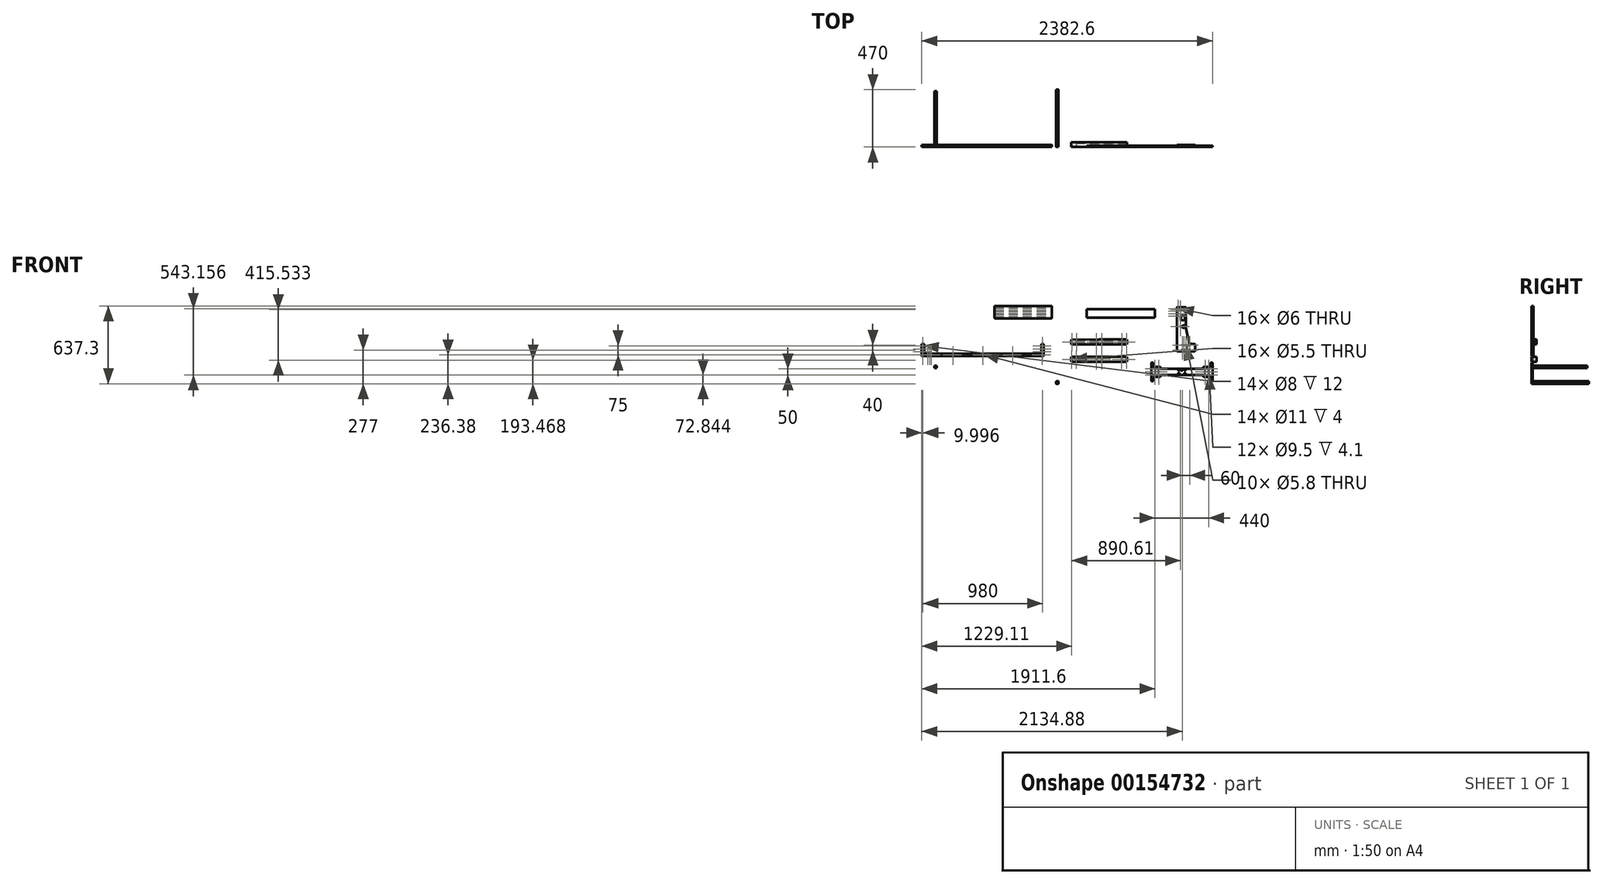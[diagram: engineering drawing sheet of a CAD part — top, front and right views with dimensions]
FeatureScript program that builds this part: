
annotation { "Feature Type Name" : "Feature", "Feature Type Description" : "" }
export const myFeature = defineFeature(function(context is Context, id is Id, definition is map)
    precondition{}
    {
        {
            var Q0;
            Q0=qCreatedBy(makeId("Front.planeOp"),FACE);
            var sketch = newSketch(context, id + "F0", { "sketchPlane" : qUnion([Q0])});
            skLineSegment(sketch, "E0.bottom", {"start": v(1.58, 127.3) * mm, "end": v(230.58, 127.3) * mm});
            skLineSegment(sketch, "E0.top", {"start": v(-227.42, 86.08) * mm, "end": v(230.58, 86.08) * mm});
            skLineSegment(sketch, "E1.0", {"start": v(225.58, 126) * mm, "end": v(225.58, 86) * mm, "construction": true});
            skLineSegment(sketch, "E2.0", {"start": v(187.58, 126) * mm, "end": v(187.58, 86) * mm, "construction": true});
            skCircle(sketch, "E3", {"center": v(187.58, 106) * mm, "radius": 2.75 * mm});
            skCircle(sketch, "E4", {"center": v(225.58, 106) * mm, "radius": 2.75 * mm});
            skLineSegment(sketch, "E5.0", {"start": v(-222.42, 126) * mm, "end": v(-222.42, 86) * mm, "construction": true});
            skLineSegment(sketch, "E6.0", {"start": v(-184.42, 126) * mm, "end": v(-184.42, 86) * mm, "construction": true});
            skCircle(sketch, "E7", {"center": v(-222.42, 106) * mm, "radius": 2.75 * mm});
            skCircle(sketch, "E8", {"center": v(-184.42, 106) * mm, "radius": 2.75 * mm});
            skLineSegment(sketch, "E9", {"start": v(1.58, 86.08) * mm, "end": v(1.58, 127.3) * mm, "construction": true});
            skLineSegment(sketch, "E10.0", {"start": v(24.58, 86) * mm, "end": v(24.58, 126) * mm, "construction": true});
            skLineSegment(sketch, "E11.0", {"start": v(-21.42, 86) * mm, "end": v(-21.42, 126) * mm, "construction": true});
            skCircle(sketch, "E12", {"center": v(24.58, 106) * mm, "radius": 3.3 * mm});
            skCircle(sketch, "E13", {"center": v(-21.42, 106) * mm, "radius": 3.3 * mm});
            skLineSegment(sketch, "E14", {"start": v(1.58, 127.3) * mm, "end": v(-227.42, 126.08) * mm});
            skLineSegment(sketch, "E15", {"start": v(-227.42, 126.08) * mm, "end": v(-227.42, 86.08) * mm});
            skLineSegment(sketch, "E16", {"start": v(230.58, 86.08) * mm, "end": v(230.58, 127.3) * mm});
            skSolve(sketch);
        }
        {
            var Q0;
            Q0=makeQuery(id+"F0.imprint","IMPRINT",FACE,{"disambiguationData":[TD([[makeQuery(id+"F0.imprint","IMPRINT",EDGE,{"derivedFrom":sQuery(id+"F0.wireOp",EDGE,"E13")}),1.0]])]});
            var Q1;
            Q1=makeQuery(id+"F0.imprint","IMPRINT",FACE,{"disambiguationData":[TD([[makeQuery(id+"F0.imprint","IMPRINT",EDGE,{"derivedFrom":sQuery(id+"F0.wireOp",EDGE,"E12")}),1.0]])]});
            var Q2;
            Q2=makeQuery(id+"F0.imprint","IMPRINT",FACE,{"disambiguationData":[TD([[makeQuery(id+"F0.imprint","IMPRINT",EDGE,{"derivedFrom":sQuery(id+"F0.wireOp",EDGE,"E8")}),1.0]])]});
            var Q3;
            Q3=makeQuery(id+"F0.imprint","IMPRINT",FACE,{"disambiguationData":[TD([[makeQuery(id+"F0.imprint","IMPRINT",EDGE,{"derivedFrom":sQuery(id+"F0.wireOp",EDGE,"E7")}),1.0]])]});
            var Q4;
            Q4=makeQuery(id+"F0.imprint","IMPRINT",FACE,{"disambiguationData":[TD([[makeQuery(id+"F0.imprint","IMPRINT",EDGE,{"derivedFrom":sQuery(id+"F0.wireOp",EDGE,"E0.bottom")}),-1.0]])]});
            var Q5;
            Q5=makeQuery(id+"F0.imprint","IMPRINT",FACE,{"disambiguationData":[TD([[makeQuery(id+"F0.imprint","IMPRINT",EDGE,{"derivedFrom":sQuery(id+"F0.wireOp",EDGE,"E3")}),1.0]])]});
            var Q6;
            Q6=makeQuery(id+"F0.imprint","IMPRINT",FACE,{"disambiguationData":[TD([[makeQuery(id+"F0.imprint","IMPRINT",EDGE,{"derivedFrom":sQuery(id+"F0.wireOp",EDGE,"E4")}),1.0]])]});
            extrude(context, id + "F1", {"entities" : qUnion([Q0, Q1, Q2, Q3, Q4, Q5, Q6]), "oppositeDirection" : true, "depth" : 40 * mm});
        }
        {
            var Q0;
            Q0=sQuery(id+"F0.wireOp",VERTEX,"E13.center");
            var Q1;
            Q1=sQuery(id+"F0.wireOp",VERTEX,"E12.center");
            var Q2;
            Q2=sQuery(id+"F0.wireOp",VERTEX,"E7.center");
            var Q3;
            Q3=sQuery(id+"F0.wireOp",VERTEX,"E8.center");
            var Q4;
            Q4=sQuery(id+"F0.wireOp",VERTEX,"E3.center");
            var Q5;
            Q5=sQuery(id+"F0.wireOp",VERTEX,"E4.center");
            var Q6;
            Q6=makeQuery(id+"F1.opExtrude","SWEPT_BODY",BODY,{"disambiguationData":[OSD([sQuery(id+"F0.wireOp",EDGE,"E0.bottom"),sQuery(id+"F0.wireOp",EDGE,"E0.top"),sQuery(id+"F0.wireOp",EDGE,"E0.left"),sQuery(id+"F0.wireOp",EDGE,"E0.right")])]});
            hole(context, id + "F2", {"style" : HoleStyle.SIMPLE, "endStyle" : HoleEndStyle.BLIND, "holeDiameter" : 5.5 * mm, "holeDepth" : 15 * mm, "locations" : qUnion([Q0, Q1, Q2, Q3, Q4, Q5]), "scope" : qUnion([Q6])});
        }
        {
            var Q0;
            Q0=makeQuery(id+"F1.opExtrude","SWEPT_FACE",FACE,{"disambiguationData":[OSD([sQuery(id+"F0.wireOp",EDGE,"E15")])]});
            var sketch = newSketch(context, id + "F3", { "sketchPlane" : qUnion([Q0])});
            skLineSegment(sketch, "E17.0", {"start": v(-20, 126.08) * mm, "end": v(-20, 86.08) * mm, "construction": true});
            skCircle(sketch, "E18", {"center": v(-30, 121.08) * mm, "radius": 3.4 * mm, "construction": true});
            skCircle(sketch, "E19.0.1.0", {"center": v(-30, 106.08) * mm, "radius": 3.4 * mm, "construction": true});
            skCircle(sketch, "E19.0.2.0", {"center": v(-30, 91.08) * mm, "radius": 3.4 * mm, "construction": true});
            skLineSegment(sketch, "E19.direction1", {"start": v(-30, 121.08) * mm, "end": v(-5, 121.08) * mm, "construction": true});
            skLineSegment(sketch, "E19.direction2", {"start": v(-30, 121.08) * mm, "end": v(-30, 106.08) * mm, "construction": true});
            skSolve(sketch);
        }
        {
            var Q0;
            Q0=sQuery(id+"F3.wireOp",VERTEX,"E18.center");
            var Q1;
            Q1=sQuery(id+"F3.wireOp",VERTEX,"E19.0.1.0.center");
            var Q2;
            Q2=sQuery(id+"F3.wireOp",VERTEX,"E19.0.2.0.center");
            var Q3;
            Q3=makeQuery(id+"F1.opExtrude","SWEPT_BODY",BODY,{"disambiguationData":[OSD([sQuery(id+"F0.wireOp",EDGE,"E0.bottom"),sQuery(id+"F0.wireOp",EDGE,"E0.top"),sQuery(id+"F0.wireOp",EDGE,"E14"),sQuery(id+"F0.wireOp",EDGE,"E15"),sQuery(id+"F0.wireOp",EDGE,"E16")])]});
            hole(context, id + "F4", {"style" : HoleStyle.SIMPLE, "endStyle" : HoleEndStyle.THROUGH, "holeDiameter" : 8 * mm, "locations" : qUnion([Q0, Q1, Q2]), "scope" : qUnion([Q3]), "isTappedThrough" : true});
        }
        {
            var Q0;
            Q0=qCreatedBy(makeId("Front.planeOp"),FACE);
            var sketch = newSketch(context, id + "F5", { "sketchPlane" : qUnion([Q0])});
            skLineSegment(sketch, "E20.bottom", {"start": v(-228.02, -16.41) * mm, "end": v(229.98, -16.41) * mm});
            skLineSegment(sketch, "E20.top", {"start": v(-228.02, -56.41) * mm, "end": v(229.98, -56.41) * mm});
            skLineSegment(sketch, "E21.0", {"start": v(224.98, -16.41) * mm, "end": v(224.98, -56.41) * mm, "construction": true});
            skLineSegment(sketch, "E22.0", {"start": v(186.98, -16.41) * mm, "end": v(186.98, -56.41) * mm, "construction": true});
            skLineSegment(sketch, "E23.0", {"start": v(-244.02, -36.41) * mm, "end": v(-185.02, -36.41) * mm, "construction": true});
            skCircle(sketch, "E24", {"center": v(186.98, -36.41) * mm, "radius": 2.75 * mm});
            skCircle(sketch, "E25", {"center": v(224.98, -36.41) * mm, "radius": 2.75 * mm});
            skLineSegment(sketch, "E26.0", {"start": v(-223.02, -16.41) * mm, "end": v(-223.02, -56.41) * mm, "construction": true});
            skLineSegment(sketch, "E27.0", {"start": v(-185.02, -16.41) * mm, "end": v(-185.02, -56.41) * mm, "construction": true});
            skCircle(sketch, "E28", {"center": v(-223.02, -36.41) * mm, "radius": 2.75 * mm});
            skCircle(sketch, "E29", {"center": v(-185.02, -36.41) * mm, "radius": 2.75 * mm});
            skLineSegment(sketch, "E30", {"start": v(0.98, -56.41) * mm, "end": v(0.98, -16.41) * mm, "construction": true});
            skLineSegment(sketch, "E31.0", {"start": v(23.98, -56.41) * mm, "end": v(23.98, -16.41) * mm, "construction": true});
            skLineSegment(sketch, "E32.0", {"start": v(-22.02, -56.41) * mm, "end": v(-22.02, -16.41) * mm, "construction": true});
            skLineSegment(sketch, "E33.trimOffspring", {"start": v(-25.32, -36.41) * mm, "end": v(27.28, -36.41) * mm, "construction": true});
            skLineSegment(sketch, "E34.trimOffspring", {"start": v(184.23, -36.41) * mm, "end": v(245.98, -36.41) * mm, "construction": true});
            skLineSegment(sketch, "E35.0", {"start": v(-25.32, -42.91) * mm, "end": v(27.28, -42.91) * mm, "construction": true});
            skLineSegment(sketch, "E36.0", {"start": v(-25.32, -29.91) * mm, "end": v(27.28, -29.91) * mm, "construction": true});
            skCircle(sketch, "E37", {"center": v(-22.02, -29.91) * mm, "radius": 3.3 * mm});
            skCircle(sketch, "E38.0.1.0", {"center": v(-22.02, -42.91) * mm, "radius": 3.3 * mm});
            skCircle(sketch, "E38.1.0.0", {"center": v(23.98, -29.91) * mm, "radius": 3.3 * mm});
            skCircle(sketch, "E38.1.1.0", {"center": v(23.98, -42.91) * mm, "radius": 3.3 * mm});
            skLineSegment(sketch, "E38.direction1", {"start": v(-22.02, -29.91) * mm, "end": v(23.98, -29.91) * mm, "construction": true});
            skLineSegment(sketch, "E38.direction2", {"start": v(-22.02, -29.91) * mm, "end": v(-22.02, -42.91) * mm, "construction": true});
            skLineSegment(sketch, "E39", {"start": v(-228.02, -16.41) * mm, "end": v(-228.02, -56.41) * mm});
            skLineSegment(sketch, "E40", {"start": v(229.98, -16.41) * mm, "end": v(229.98, -56.41) * mm});
            skSolve(sketch);
        }
        {
            var Q0;
            Q0=makeQuery(id+"F5.imprint","IMPRINT",FACE,{"disambiguationData":[TD([[makeQuery(id+"F5.imprint","IMPRINT",EDGE,{"derivedFrom":sQuery(id+"F5.wireOp",EDGE,"E38.1.1.0")}),1.0]])]});
            var Q1;
            Q1=makeQuery(id+"F5.imprint","IMPRINT",FACE,{"disambiguationData":[TD([[makeQuery(id+"F5.imprint","IMPRINT",EDGE,{"derivedFrom":sQuery(id+"F5.wireOp",EDGE,"E38.1.0.0")}),1.0]])]});
            var Q2;
            Q2=makeQuery(id+"F5.imprint","IMPRINT",FACE,{"disambiguationData":[TD([[makeQuery(id+"F5.imprint","IMPRINT",EDGE,{"derivedFrom":sQuery(id+"F5.wireOp",EDGE,"E37")}),1.0]])]});
            var Q3;
            Q3=makeQuery(id+"F5.imprint","IMPRINT",FACE,{"disambiguationData":[TD([[makeQuery(id+"F5.imprint","IMPRINT",EDGE,{"derivedFrom":sQuery(id+"F5.wireOp",EDGE,"E38.0.1.0")}),1.0]])]});
            var Q4;
            Q4=makeQuery(id+"F5.imprint","IMPRINT",FACE,{"disambiguationData":[TD([[makeQuery(id+"F5.imprint","IMPRINT",EDGE,{"derivedFrom":sQuery(id+"F5.wireOp",EDGE,"E24")}),1.0]])]});
            var Q5;
            Q5=makeQuery(id+"F5.imprint","IMPRINT",FACE,{"disambiguationData":[TD([[makeQuery(id+"F5.imprint","IMPRINT",EDGE,{"derivedFrom":sQuery(id+"F5.wireOp",EDGE,"E25")}),1.0]])]});
            var Q6;
            Q6=makeQuery(id+"F5.imprint","IMPRINT",FACE,{"disambiguationData":[TD([[makeQuery(id+"F5.imprint","IMPRINT",EDGE,{"derivedFrom":sQuery(id+"F5.wireOp",EDGE,"E29")}),1.0]])]});
            var Q7;
            Q7=makeQuery(id+"F5.imprint","IMPRINT",FACE,{"disambiguationData":[TD([[makeQuery(id+"F5.imprint","IMPRINT",EDGE,{"derivedFrom":sQuery(id+"F5.wireOp",EDGE,"E20.bottom")}),-1.0]])]});
            var Q8;
            Q8=makeQuery(id+"F5.imprint","IMPRINT",FACE,{"disambiguationData":[TD([[makeQuery(id+"F5.imprint","IMPRINT",EDGE,{"derivedFrom":sQuery(id+"F5.wireOp",EDGE,"E28")}),1.0]])]});
            extrude(context, id + "F6", {"entities" : qUnion([Q0, Q1, Q2, Q3, Q4, Q5, Q6, Q7, Q8]), "oppositeDirection" : true, "depth" : 40 * mm});
        }
        {
            var Q0;
            Q0=sQuery(id+"F5.wireOp",VERTEX,"E28.center");
            var Q1;
            Q1=sQuery(id+"F5.wireOp",VERTEX,"E23.0.end");
            var Q2;
            Q2=sQuery(id+"F5.wireOp",VERTEX,"E38.direction2.end");
            var Q3;
            Q3=sQuery(id+"F5.wireOp",VERTEX,"E37.center");
            var Q4;
            Q4=sQuery(id+"F5.wireOp",VERTEX,"E38.direction1.end");
            var Q5;
            Q5=sQuery(id+"F5.wireOp",VERTEX,"E38.1.1.0.center");
            var Q6;
            Q6=sQuery(id+"F5.wireOp",VERTEX,"E24.center");
            var Q7;
            Q7=sQuery(id+"F5.wireOp",VERTEX,"E25.center");
            var Q8;
            Q8=makeQuery(id+"F6.opExtrude","SWEPT_BODY",BODY,{"disambiguationData":[OSD([sQuery(id+"F5.wireOp",EDGE,"E20.bottom"),sQuery(id+"F5.wireOp",EDGE,"E20.top"),sQuery(id+"F5.wireOp",EDGE,"E20.left"),sQuery(id+"F5.wireOp",EDGE,"E20.right")])]});
            hole(context, id + "F7", {"style" : HoleStyle.SIMPLE, "endStyle" : HoleEndStyle.BLIND, "holeDiameter" : 5.5 * mm, "holeDepth" : 15 * mm, "locations" : qUnion([Q0, Q1, Q2, Q3, Q4, Q5, Q6, Q7]), "scope" : qUnion([Q8])});
        }
        {
            var Q0;
            Q0=qCreatedBy(makeId("Front.planeOp"),FACE);
            var sketch = newSketch(context, id + "F8", { "sketchPlane" : qUnion([Q0])});
            skLineSegment(sketch, "E41.bottom", {"start": v(-101.39, 376.02) * mm, "end": v(458.61, 376.02) * mm});
            skLineSegment(sketch, "E41.top", {"start": v(-101.39, 306.02) * mm, "end": v(458.61, 306.02) * mm});
            skLineSegment(sketch, "E41.left", {"start": v(-101.39, 376.02) * mm, "end": v(-101.39, 306.02) * mm});
            skLineSegment(sketch, "E41.right", {"start": v(458.61, 376.02) * mm, "end": v(458.61, 306.02) * mm});
            skSolve(sketch);
        }
        {
            var Q0;
            Q0 = qSketchRegion(id + "F8", true);
            extrude(context, id + "F9", {"entities" : qUnion([Q0]), "oppositeDirection" : true, "depth" : 10 * mm});
        }
        {
            var Q0;
            Q0=qCreatedBy(makeId("Front.planeOp"),FACE);
            var sketch = newSketch(context, id + "F10", { "sketchPlane" : qUnion([Q0])});
            skLineSegment(sketch, "E42.bottom", {"start": v(782.75, 30.62) * mm, "end": v(642.75, 30.62) * mm});
            skLineSegment(sketch, "E42.top", {"start": v(782.75, 90.62) * mm, "end": v(762.72, 90.62) * mm});
            skLineSegment(sketch, "E42.left", {"start": v(787.75, 35.62) * mm, "end": v(787.75, 85.62) * mm});
            skLineSegment(sketch, "E42.right", {"start": v(637.75, 35.62) * mm, "end": v(637.75, 90.62) * mm});
            skLineSegment(sketch, "E43.top", {"start": v(639.25, 390.62) * mm, "end": v(711.25, 390.62) * mm});
            skLineSegment(sketch, "E43.left", {"start": v(637.75, 90.62) * mm, "end": v(637.75, 389.12) * mm});
            skLineSegment(sketch, "E43.right", {"start": v(712.75, 228.87) * mm, "end": v(712.75, 389.12) * mm});
            skLineSegment(sketch, "E44.0", {"start": v(737.75, 30.62) * mm, "end": v(737.75, 90.62) * mm, "construction": true});
            skLineSegment(sketch, "E45", {"start": v(713.25, 223.43) * mm, "end": v(733.22, 115.18) * mm});
            skPoint(sketch, "E46.trimOffspring.start.orphan", {"position": v(712.75, 61.64) * mm});
            skPoint(sketch, "E47.visualSharp", {"position": v(712.75, 226.13) * mm});
            skArc(sketch, "E47.filletArc", {"start": v(712.75, 228.87) * mm, "mid": v(712.87, 226.14) * mm, "end": v(713.25, 223.43) * mm});
            skPoint(sketch, "E48.visualSharp", {"position": v(737.75, 90.62) * mm});
            skArc(sketch, "E48.filletArc", {"start": v(733.22, 115.18) * mm, "mid": v(743.53, 97.56) * mm, "end": v(762.72, 90.62) * mm});
            skPoint(sketch, "E49.visualSharp", {"position": v(637.75, 30.62) * mm});
            skArc(sketch, "E49.filletArc", {"start": v(637.75, 35.62) * mm, "mid": v(639.21, 32.08) * mm, "end": v(642.75, 30.62) * mm});
            skPoint(sketch, "E50.visualSharp", {"position": v(787.75, 30.62) * mm});
            skArc(sketch, "E50.filletArc", {"start": v(782.75, 30.62) * mm, "mid": v(786.28, 32.08) * mm, "end": v(787.75, 35.62) * mm});
            skPoint(sketch, "E51.visualSharp", {"position": v(787.75, 90.62) * mm});
            skArc(sketch, "E51.filletArc", {"start": v(787.75, 85.62) * mm, "mid": v(786.28, 89.16) * mm, "end": v(782.75, 90.62) * mm});
            skPoint(sketch, "E52.visualSharp", {"position": v(637.75, 390.62) * mm});
            skArc(sketch, "E52.filletArc", {"start": v(639.25, 390.62) * mm, "mid": v(638.19, 390.18) * mm, "end": v(637.75, 389.12) * mm});
            skPoint(sketch, "E53.visualSharp", {"position": v(712.75, 390.62) * mm});
            skArc(sketch, "E53.filletArc", {"start": v(712.75, 389.12) * mm, "mid": v(712.3, 390.18) * mm, "end": v(711.25, 390.62) * mm});
            skLineSegment(sketch, "E54", {"start": v(712.75, 30.62) * mm, "end": v(712.75, 106.15) * mm, "construction": true});
            skLineSegment(sketch, "E55.0", {"start": v(782.75, 60.62) * mm, "end": v(642.75, 60.62) * mm, "construction": true});
            skLineSegment(sketch, "E56.bottom", {"start": v(682.75, 80.62) * mm, "end": v(742.75, 80.62) * mm, "construction": true});
            skLineSegment(sketch, "E56.top", {"start": v(682.75, 40.62) * mm, "end": v(742.75, 40.62) * mm, "construction": true});
            skLineSegment(sketch, "E56.left", {"start": v(682.75, 80.62) * mm, "end": v(682.75, 40.62) * mm, "construction": true});
            skLineSegment(sketch, "E56.right", {"start": v(742.75, 80.62) * mm, "end": v(742.75, 40.62) * mm, "construction": true});
            skPoint(sketch, "E56.middle", {"position": v(712.75, 60.62) * mm});
            skCircle(sketch, "E57", {"center": v(682.75, 80.62) * mm, "radius": 2.9 * mm, "construction": true});
            skCircle(sketch, "E58.0.1.0", {"center": v(682.75, 40.62) * mm, "radius": 2.9 * mm, "construction": true});
            skCircle(sketch, "E58.1.0.0", {"center": v(697.75, 80.62) * mm, "radius": 2.9 * mm, "construction": true});
            skCircle(sketch, "E58.1.1.0", {"center": v(697.75, 40.62) * mm, "radius": 2.9 * mm, "construction": true});
            skCircle(sketch, "E58.2.0.0", {"center": v(712.75, 80.62) * mm, "radius": 2.9 * mm, "construction": true});
            skCircle(sketch, "E58.2.1.0", {"center": v(712.75, 40.62) * mm, "radius": 2.9 * mm, "construction": true});
            skCircle(sketch, "E58.3.0.0", {"center": v(727.75, 80.62) * mm, "radius": 2.9 * mm, "construction": true});
            skCircle(sketch, "E58.3.1.0", {"center": v(727.75, 40.62) * mm, "radius": 2.9 * mm, "construction": true});
            skCircle(sketch, "E58.4.0.0", {"center": v(742.75, 80.62) * mm, "radius": 2.9 * mm, "construction": true});
            skCircle(sketch, "E58.4.1.0", {"center": v(742.75, 40.62) * mm, "radius": 2.9 * mm, "construction": true});
            skLineSegment(sketch, "E58.direction1", {"start": v(682.75, 80.62) * mm, "end": v(697.75, 80.62) * mm, "construction": true});
            skLineSegment(sketch, "E59.0", {"start": v(659.75, 90.62) * mm, "end": v(659.75, 389.12) * mm, "construction": true});
            skLineSegment(sketch, "E60.bottom", {"start": v(1072.94, 142.18) * mm, "end": v(932.94, 142.18) * mm});
            skLineSegment(sketch, "E60.top", {"start": v(1072.94, 202.18) * mm, "end": v(1053.84, 202.18) * mm});
            skLineSegment(sketch, "E60.left", {"start": v(1077.94, 147.18) * mm, "end": v(1077.94, 197.18) * mm});
            skLineSegment(sketch, "E60.right", {"start": v(927.94, 147.18) * mm, "end": v(927.94, 202.18) * mm});
            skLineSegment(sketch, "E61.top", {"start": v(929.44, 502.18) * mm, "end": v(1006.44, 502.18) * mm});
            skLineSegment(sketch, "E61.left", {"start": v(927.94, 202.18) * mm, "end": v(927.94, 500.68) * mm});
            skLineSegment(sketch, "E61.right", {"start": v(1007.94, 339.89) * mm, "end": v(1007.94, 500.68) * mm});
            skLineSegment(sketch, "E62.0", {"start": v(1027.94, 142.18) * mm, "end": v(1027.94, 202.18) * mm, "construction": true});
            skLineSegment(sketch, "E63", {"start": v(1008.26, 335.5) * mm, "end": v(1024.16, 227.8) * mm});
            skPoint(sketch, "E64.trimOffspring.start.orphan", {"position": v(1007.94, 173.2) * mm});
            skPoint(sketch, "E65.visualSharp", {"position": v(1007.94, 337.69) * mm});
            skArc(sketch, "E65.filletArc", {"start": v(1007.94, 339.89) * mm, "mid": v(1008.02, 337.7) * mm, "end": v(1008.26, 335.5) * mm});
            skPoint(sketch, "E66.visualSharp", {"position": v(1027.94, 202.18) * mm});
            skArc(sketch, "E66.filletArc", {"start": v(1024.16, 227.8) * mm, "mid": v(1034.23, 209.47) * mm, "end": v(1053.84, 202.18) * mm});
            skPoint(sketch, "E67.visualSharp", {"position": v(927.94, 142.18) * mm});
            skArc(sketch, "E67.filletArc", {"start": v(927.94, 147.18) * mm, "mid": v(929.4, 143.64) * mm, "end": v(932.94, 142.18) * mm});
            skPoint(sketch, "E68.visualSharp", {"position": v(1077.94, 142.18) * mm});
            skArc(sketch, "E68.filletArc", {"start": v(1072.94, 142.18) * mm, "mid": v(1076.47, 143.64) * mm, "end": v(1077.94, 147.18) * mm});
            skPoint(sketch, "E69.visualSharp", {"position": v(1077.94, 202.18) * mm});
            skArc(sketch, "E69.filletArc", {"start": v(1077.94, 197.18) * mm, "mid": v(1076.47, 200.71) * mm, "end": v(1072.94, 202.18) * mm});
            skPoint(sketch, "E70.visualSharp", {"position": v(927.94, 502.18) * mm});
            skArc(sketch, "E70.filletArc", {"start": v(929.44, 502.18) * mm, "mid": v(928.38, 501.74) * mm, "end": v(927.94, 500.68) * mm});
            skPoint(sketch, "E71.visualSharp", {"position": v(1007.94, 502.18) * mm});
            skArc(sketch, "E71.filletArc", {"start": v(1007.94, 500.68) * mm, "mid": v(1007.5, 501.74) * mm, "end": v(1006.44, 502.18) * mm});
            skLineSegment(sketch, "E72", {"start": v(1002.94, 142.18) * mm, "end": v(1002.94, 217.7) * mm, "construction": true});
            skLineSegment(sketch, "E73.0", {"start": v(1072.94, 172.18) * mm, "end": v(932.94, 172.18) * mm, "construction": true});
            skLineSegment(sketch, "E74.bottom", {"start": v(972.94, 192.18) * mm, "end": v(1032.94, 192.18) * mm, "construction": true});
            skLineSegment(sketch, "E74.top", {"start": v(972.94, 152.18) * mm, "end": v(1032.94, 152.18) * mm, "construction": true});
            skLineSegment(sketch, "E74.left", {"start": v(972.94, 192.18) * mm, "end": v(972.94, 152.18) * mm, "construction": true});
            skLineSegment(sketch, "E74.right", {"start": v(1032.94, 192.18) * mm, "end": v(1032.94, 152.18) * mm, "construction": true});
            skPoint(sketch, "E74.middle", {"position": v(1002.94, 172.18) * mm});
            skCircle(sketch, "E75", {"center": v(972.94, 192.18) * mm, "radius": 2.9 * mm, "construction": true});
            skCircle(sketch, "E76.0.1.0", {"center": v(972.94, 152.18) * mm, "radius": 2.9 * mm, "construction": true});
            skCircle(sketch, "E76.1.0.0", {"center": v(987.94, 192.18) * mm, "radius": 2.9 * mm, "construction": true});
            skCircle(sketch, "E76.1.1.0", {"center": v(987.94, 152.18) * mm, "radius": 2.9 * mm, "construction": true});
            skCircle(sketch, "E76.2.0.0", {"center": v(1002.94, 192.18) * mm, "radius": 2.9 * mm, "construction": true});
            skCircle(sketch, "E76.2.1.0", {"center": v(1002.94, 152.18) * mm, "radius": 2.9 * mm, "construction": true});
            skCircle(sketch, "E76.3.0.0", {"center": v(1017.94, 192.18) * mm, "radius": 2.9 * mm, "construction": true});
            skCircle(sketch, "E76.3.1.0", {"center": v(1017.94, 152.18) * mm, "radius": 2.9 * mm, "construction": true});
            skCircle(sketch, "E76.4.0.0", {"center": v(1032.94, 192.18) * mm, "radius": 2.9 * mm, "construction": true});
            skCircle(sketch, "E76.4.1.0", {"center": v(1032.94, 152.18) * mm, "radius": 2.9 * mm, "construction": true});
            skLineSegment(sketch, "E76.direction1", {"start": v(972.94, 192.18) * mm, "end": v(987.94, 192.18) * mm, "construction": true});
            skLineSegment(sketch, "E77.0", {"start": v(947.94, 202.18) * mm, "end": v(947.94, 500.68) * mm, "construction": true});
            skLineSegment(sketch, "E78.0", {"start": v(639.25, 379.62) * mm, "end": v(716.25, 379.62) * mm, "construction": true});
            skLineSegment(sketch, "E79.0", {"start": v(648.75, 90.62) * mm, "end": v(648.75, 389.12) * mm, "construction": true});
            skCircle(sketch, "E80", {"center": v(648.75, 379.62) * mm, "radius": 3 * mm});
            skLineSegment(sketch, "E81.direction1", {"start": v(648.75, 379.62) * mm, "end": v(659.75, 379.62) * mm, "construction": true});
            skCircle(sketch, "E82.0.1.0", {"center": v(648.75, 359.12) * mm, "radius": 3 * mm});
            skCircle(sketch, "E82.0.2.0", {"center": v(648.75, 338.62) * mm, "radius": 3 * mm});
            skCircle(sketch, "E82.0.3.0", {"center": v(648.75, 318.12) * mm, "radius": 3 * mm});
            skLineSegment(sketch, "E82.direction1", {"start": v(648.75, 379.62) * mm, "end": v(668.75, 379.62) * mm, "construction": true});
            skLineSegment(sketch, "E82.direction2", {"start": v(648.75, 379.62) * mm, "end": v(648.75, 359.12) * mm, "construction": true});
            skPoint(sketch, "E83.middle", {"position": v(687.75, 372.62) * mm});
            skCircle(sketch, "E84", {"center": v(687.75, 372.62) * mm, "radius": 8 * mm});
            skCircle(sketch, "E85", {"center": v(687.75, 372.62) * mm, "radius": 14 * mm});
            skLineSegment(sketch, "E86.left", {"start": v(712.75, 370.62) * mm, "end": v(712.75, 374.62) * mm});
            skLineSegment(sketch, "E86.right", {"start": v(662.75, 370.62) * mm, "end": v(662.75, 374.62) * mm});
            skCircle(sketch, "E87", {"center": v(667.56, 372.62) * mm, "radius": 2.75 * mm});
            skCircle(sketch, "E88", {"center": v(707.75, 372.62) * mm, "radius": 2.75 * mm});
            skLineSegment(sketch, "E89", {"start": v(712.75, 374.62) * mm, "end": v(694.61, 384.82) * mm});
            skLineSegment(sketch, "E90", {"start": v(712.75, 370.62) * mm, "end": v(694.61, 360.42) * mm});
            skLineSegment(sketch, "E91", {"start": v(662.75, 370.62) * mm, "end": v(680.88, 360.42) * mm});
            skLineSegment(sketch, "E92", {"start": v(662.75, 374.62) * mm, "end": v(680.88, 384.82) * mm});
            skLineSegment(sketch, "E93", {"start": v(680.88, 384.82) * mm, "end": v(680.88, 389.62) * mm});
            skLineSegment(sketch, "E94", {"start": v(694.61, 384.82) * mm, "end": v(694.61, 389.62) * mm});
            skLineSegment(sketch, "E95", {"start": v(694.61, 389.62) * mm, "end": v(680.88, 389.62) * mm});
            skPoint(sketch, "E96.middle", {"position": v(759.9, 318.54) * mm});
            skCircle(sketch, "E97", {"center": v(759.9, 318.54) * mm, "radius": 8 * mm});
            skCircle(sketch, "E98", {"center": v(759.9, 318.54) * mm, "radius": 14 * mm});
            skLineSegment(sketch, "E99.left", {"start": v(784.9, 316.54) * mm, "end": v(784.9, 320.54) * mm});
            skLineSegment(sketch, "E99.right", {"start": v(734.9, 316.54) * mm, "end": v(734.9, 320.54) * mm});
            skCircle(sketch, "E100", {"center": v(739.9, 318.54) * mm, "radius": 2.75 * mm});
            skCircle(sketch, "E101", {"center": v(779.9, 318.54) * mm, "radius": 2.75 * mm});
            skLineSegment(sketch, "E102", {"start": v(784.9, 320.54) * mm, "end": v(766.77, 330.74) * mm});
            skLineSegment(sketch, "E103", {"start": v(784.9, 316.54) * mm, "end": v(766.77, 306.34) * mm});
            skLineSegment(sketch, "E104", {"start": v(734.9, 316.54) * mm, "end": v(753.04, 306.34) * mm});
            skLineSegment(sketch, "E105", {"start": v(734.9, 320.54) * mm, "end": v(753.04, 330.74) * mm});
            skLineSegment(sketch, "E106", {"start": v(753.04, 330.74) * mm, "end": v(753.04, 335.54) * mm});
            skLineSegment(sketch, "E107", {"start": v(766.77, 330.74) * mm, "end": v(766.77, 335.54) * mm});
            skLineSegment(sketch, "E108", {"start": v(766.77, 335.54) * mm, "end": v(753.04, 335.54) * mm});
            skPoint(sketch, "E109.middle", {"position": v(687.75, 232.62) * mm});
            skCircle(sketch, "E110", {"center": v(687.75, 232.62) * mm, "radius": 8 * mm});
            skCircle(sketch, "E111", {"center": v(687.75, 232.62) * mm, "radius": 14 * mm});
            skLineSegment(sketch, "E112.left", {"start": v(712.75, 230.62) * mm, "end": v(712.75, 234.62) * mm});
            skLineSegment(sketch, "E112.right", {"start": v(662.75, 230.62) * mm, "end": v(662.75, 234.62) * mm});
            skCircle(sketch, "E113", {"center": v(667.6, 232.62) * mm, "radius": 2.75 * mm});
            skCircle(sketch, "E114", {"center": v(707.75, 232.62) * mm, "radius": 2.75 * mm});
            skLineSegment(sketch, "E115", {"start": v(712.75, 234.62) * mm, "end": v(694.61, 244.82) * mm});
            skLineSegment(sketch, "E116", {"start": v(712.75, 230.62) * mm, "end": v(694.61, 220.42) * mm});
            skLineSegment(sketch, "E117", {"start": v(662.75, 230.62) * mm, "end": v(680.88, 220.42) * mm});
            skLineSegment(sketch, "E118", {"start": v(662.75, 234.62) * mm, "end": v(680.88, 244.82) * mm});
            skLineSegment(sketch, "E119", {"start": v(680.88, 244.82) * mm, "end": v(680.88, 249.62) * mm});
            skLineSegment(sketch, "E120", {"start": v(694.61, 244.82) * mm, "end": v(694.61, 249.62) * mm});
            skLineSegment(sketch, "E121", {"start": v(694.61, 249.62) * mm, "end": v(680.88, 249.62) * mm});
            skLineSegment(sketch, "E122.bottom", {"start": v(709.75, 280.62) * mm, "end": v(665.75, 280.62) * mm});
            skLineSegment(sketch, "E122.top", {"start": v(709.75, 324.62) * mm, "end": v(665.75, 324.62) * mm});
            skLineSegment(sketch, "E122.left", {"start": v(709.75, 280.62) * mm, "end": v(709.75, 324.62) * mm});
            skLineSegment(sketch, "E122.right", {"start": v(665.75, 280.62) * mm, "end": v(665.75, 324.62) * mm});
            skPoint(sketch, "E122.middle", {"position": v(687.75, 302.62) * mm});
            skCircle(sketch, "E123", {"center": v(687.75, 302.62) * mm, "radius": 22 * mm, "construction": true});
            skLineSegment(sketch, "E124", {"start": v(709.75, 280.62) * mm, "end": v(665.75, 324.62) * mm, "construction": true});
            skLineSegment(sketch, "E125", {"start": v(665.75, 280.62) * mm, "end": v(709.75, 324.62) * mm, "construction": true});
            skCircle(sketch, "E126", {"center": v(672.2, 318.18) * mm, "radius": 4 * mm, "construction": true});
            skCircle(sketch, "E127", {"center": v(703.3, 318.18) * mm, "radius": 4 * mm, "construction": true});
            skCircle(sketch, "E128", {"center": v(703.3, 287.06) * mm, "radius": 4 * mm, "construction": true});
            skCircle(sketch, "E129", {"center": v(672.2, 287.06) * mm, "radius": 4 * mm, "construction": true});
            skCircle(sketch, "E130", {"center": v(687.75, 302.62) * mm, "radius": 18 * mm});
            skLineSegment(sketch, "E131", {"start": v(687.75, 232.62) * mm, "end": v(687.75, 390.62) * mm, "construction": true});
            skSolve(sketch);
        }
        {
            var Q0;
            Q0=makeQuery(id+"F10.imprint","IMPRINT",FACE,{"disambiguationData":[TD([[makeQuery(id+"F10.imprint","IMPRINT",EDGE,{"derivedFrom":sQuery(id+"F10.wireOp",EDGE,"E42.bottom")}),-1.0]])]});
            var Q1;
            Q1=makeQuery(id+"F10.imprint","IMPRINT",FACE,{"disambiguationData":[TD([[makeQuery(id+"F10.imprint","IMPRINT",EDGE,{"derivedFrom":sQuery(id+"F10.wireOp",EDGE,"E84")}),-1.0]])]});
            var Q2;
            Q2=makeQuery(id+"F10.imprint","IMPRINT",FACE,{"disambiguationData":[TD([[makeQuery(id+"F10.imprint","IMPRINT",EDGE,{"derivedFrom":sQuery(id+"F10.wireOp",EDGE,"E86.left")}),1.0]])]});
            var Q3;
            Q3=makeQuery(id+"F10.imprint","IMPRINT",FACE,{"disambiguationData":[TD([[makeQuery(id+"F10.imprint","IMPRINT",EDGE,{"derivedFrom":sQuery(id+"F10.wireOp",EDGE,"E86.right")}),-1.0]])]});
            var Q4;
            {var subQ2=sQuery(id+"F10.wireOp",EDGE,"E93");Q4=makeQuery(id+"F10.imprint","IMPRINT",FACE,{"disambiguationData":[TD([[makeQuery(id+"F10.imprint","IMPRINT",EDGE,{"derivedFrom":subQ2}),-1.0]])]});}
            var Q5;
            Q5=makeQuery(id+"F10.imprint","IMPRINT",FACE,{"disambiguationData":[TD([[makeQuery(id+"F10.imprint","IMPRINT",EDGE,{"derivedFrom":sQuery(id+"F10.wireOp",EDGE,"E110")}),-1.0]])]});
            var Q6;
            Q6=makeQuery(id+"F10.imprint","IMPRINT",FACE,{"disambiguationData":[TD([[makeQuery(id+"F10.imprint","IMPRINT",EDGE,{"derivedFrom":sQuery(id+"F10.wireOp",EDGE,"E112.left")}),1.0]])]});
            var Q7;
            {var subQ2=sQuery(id+"F10.wireOp",EDGE,"E119");Q7=makeQuery(id+"F10.imprint","IMPRINT",FACE,{"disambiguationData":[TD([[makeQuery(id+"F10.imprint","IMPRINT",EDGE,{"derivedFrom":subQ2}),-1.0]])]});}
            var Q8;
            Q8=makeQuery(id+"F10.imprint","IMPRINT",FACE,{"disambiguationData":[TD([[makeQuery(id+"F10.imprint","IMPRINT",EDGE,{"derivedFrom":sQuery(id+"F10.wireOp",EDGE,"E112.right")}),-1.0]])]});
            var Q9;
            Q9=makeQuery(id+"F10.imprint","IMPRINT",FACE,{"disambiguationData":[TD([[makeQuery(id+"F10.imprint","IMPRINT",EDGE,{"derivedFrom":sQuery(id+"F10.wireOp",EDGE,"E122.bottom")}),-1.0]])]});
            extrude(context, id + "F11", {"entities" : qUnion([Q0, Q1, Q2, Q3, Q4, Q5, Q6, Q7, Q8, Q9]), "oppositeDirection" : true, "depth" : 16 * mm});
        }
        {
            var Q0;
            Q0=sQuery(id+"F10.wireOp",VERTEX,"E57.center");
            var Q1;
            Q1=sQuery(id+"F10.wireOp",VERTEX,"E58.1.0.0.center");
            var Q2;
            Q2=sQuery(id+"F10.wireOp",VERTEX,"E58.2.0.0.center");
            var Q3;
            Q3=sQuery(id+"F10.wireOp",VERTEX,"E58.3.0.0.center");
            var Q4;
            Q4=sQuery(id+"F10.wireOp",VERTEX,"E56.right.start");
            var Q5;
            Q5=sQuery(id+"F10.wireOp",VERTEX,"E58.4.1.0.center");
            var Q6;
            Q6=sQuery(id+"F10.wireOp",VERTEX,"E58.3.1.0.center");
            var Q7;
            Q7=sQuery(id+"F10.wireOp",VERTEX,"E58.2.1.0.center");
            var Q8;
            Q8=sQuery(id+"F10.wireOp",VERTEX,"E58.1.1.0.center");
            var Q9;
            Q9=sQuery(id+"F10.wireOp",VERTEX,"E56.left.end");
            var Q10;
            Q10=makeQuery(id+"F11.opExtrude","SWEPT_BODY",BODY,{"disambiguationData":[OSD([sQuery(id+"F10.wireOp",EDGE,"E42.bottom"),sQuery(id+"F10.wireOp",EDGE,"E42.top"),sQuery(id+"F10.wireOp",EDGE,"E42.left"),sQuery(id+"F10.wireOp",EDGE,"E42.right"),sQuery(id+"F10.wireOp",EDGE,"E43.top"),sQuery(id+"F10.wireOp",EDGE,"E43.left"),sQuery(id+"F10.wireOp",EDGE,"E43.right"),sQuery(id+"F10.wireOp",EDGE,"E45"),sQuery(id+"F10.wireOp",EDGE,"E47.filletArc"),sQuery(id+"F10.wireOp",EDGE,"E48.filletArc"),sQuery(id+"F10.wireOp",EDGE,"E49.filletArc"),sQuery(id+"F10.wireOp",EDGE,"E50.filletArc"),sQuery(id+"F10.wireOp",EDGE,"E51.filletArc"),sQuery(id+"F10.wireOp",EDGE,"E52.filletArc"),sQuery(id+"F10.wireOp",EDGE,"E53.filletArc")])]});
            hole(context, id + "F12", {"style" : HoleStyle.SIMPLE, "endStyle" : HoleEndStyle.THROUGH, "holeDiameter" : 5.8 * mm, "locations" : qUnion([Q0, Q1, Q2, Q3, Q4, Q5, Q6, Q7, Q8, Q9]), "scope" : qUnion([Q10]), "isTappedThrough" : true});
        }
        {
            var Q0;
            Q0=sQuery(id+"F10.wireOp",VERTEX,"E127.center");
            var Q1;
            Q1=sQuery(id+"F10.wireOp",VERTEX,"E128.center");
            var Q2;
            Q2=sQuery(id+"F10.wireOp",VERTEX,"E129.center");
            var Q3;
            Q3=sQuery(id+"F10.wireOp",VERTEX,"E126.center");
            var Q4;
            Q4=makeQuery(id+"F11.opExtrude","SWEPT_BODY",BODY,{"disambiguationData":[OSD([sQuery(id+"F10.wireOp",EDGE,"E42.bottom"),sQuery(id+"F10.wireOp",EDGE,"E42.top"),sQuery(id+"F10.wireOp",EDGE,"E42.left"),sQuery(id+"F10.wireOp",EDGE,"E42.right"),sQuery(id+"F10.wireOp",EDGE,"E43.top"),sQuery(id+"F10.wireOp",EDGE,"E43.left"),sQuery(id+"F10.wireOp",EDGE,"E43.right"),sQuery(id+"F10.wireOp",EDGE,"E45"),sQuery(id+"F10.wireOp",EDGE,"E47.filletArc"),sQuery(id+"F10.wireOp",EDGE,"E48.filletArc"),sQuery(id+"F10.wireOp",EDGE,"E49.filletArc"),sQuery(id+"F10.wireOp",EDGE,"E50.filletArc"),sQuery(id+"F10.wireOp",EDGE,"E51.filletArc"),sQuery(id+"F10.wireOp",EDGE,"E52.filletArc"),sQuery(id+"F10.wireOp",EDGE,"E53.filletArc"),sQuery(id+"F10.wireOp",EDGE,"E80"),sQuery(id+"F10.wireOp",EDGE,"E82.0.1.0"),sQuery(id+"F10.wireOp",EDGE,"E82.0.2.0"),sQuery(id+"F10.wireOp",EDGE,"E82.0.3.0"),sQuery(id+"F10.wireOp",EDGE,"E82.1.0.0"),sQuery(id+"F10.wireOp",EDGE,"E82.2.0.0"),sQuery(id+"F10.wireOp",EDGE,"E82.3.0.0"),sQuery(id+"F10.wireOp",EDGE,"E84"),sQuery(id+"F10.wireOp",EDGE,"E87"),sQuery(id+"F10.wireOp",EDGE,"E88"),sQuery(id+"F10.wireOp",EDGE,"E110"),sQuery(id+"F10.wireOp",EDGE,"E113"),sQuery(id+"F10.wireOp",EDGE,"E114"),sQuery(id+"F10.wireOp",EDGE,"E130")])]});
            hole(context, id + "F13", {"style" : HoleStyle.SIMPLE, "endStyle" : HoleEndStyle.THROUGH, "holeDiameter" : 4 * mm, "locations" : qUnion([Q0, Q1, Q2, Q3]), "scope" : qUnion([Q4]), "isTappedThrough" : true});
        }
        {
            var Q0;
            Q0=qCreatedBy(makeId("Front.planeOp"),FACE);
            var sketch = newSketch(context, id + "F14", { "sketchPlane" : qUnion([Q0])});
            skLineSegment(sketch, "E132.bottom", {"start": v(444.47, -213.54) * mm, "end": v(428.47, -213.54) * mm});
            skLineSegment(sketch, "E132.top", {"start": v(444.47, -63.54) * mm, "end": v(428.47, -63.54) * mm});
            skLineSegment(sketch, "E132.left", {"start": v(444.47, -213.54) * mm, "end": v(444.47, -178.54) * mm});
            skLineSegment(sketch, "E132.right", {"start": v(428.47, -213.54) * mm, "end": v(428.47, -63.54) * mm});
            skPoint(sketch, "E132.middle", {"position": v(436.47, -138.54) * mm});
            skLineSegment(sketch, "E133", {"start": v(428.47, -138.54) * mm, "end": v(889.76, -138.54) * mm, "construction": true});
            skPoint(sketch, "E133.endSnap0", {"position": v(428.47, -138.54) * mm});
            skLineSegment(sketch, "E134.bottom", {"start": v(504.47, -178.54) * mm, "end": v(444.47, -178.54) * mm});
            skLineSegment(sketch, "E134.top", {"start": v(504.47, -98.54) * mm, "end": v(444.47, -98.54) * mm});
            skLineSegment(sketch, "E134.left", {"start": v(504.47, -178.54) * mm, "end": v(504.47, -163.54) * mm});
            skPoint(sketch, "E134.middle", {"position": v(444.47, -138.54) * mm});
            skLineSegment(sketch, "E135.trimOffspring", {"start": v(444.47, -98.54) * mm, "end": v(444.47, -63.54) * mm});
            skPoint(sketch, "E136.middle", {"position": v(504.47, -138.54) * mm});
            skLineSegment(sketch, "E137.bottom", {"start": v(679.47, -163.54) * mm, "end": v(504.47, -163.54) * mm});
            skLineSegment(sketch, "E137.top", {"start": v(679.47, -113.54) * mm, "end": v(504.47, -113.54) * mm});
            skLineSegment(sketch, "E137.left", {"start": v(679.47, -163.54) * mm, "end": v(679.47, -113.54) * mm});
            skLineSegment(sketch, "E138.trimOffspring", {"start": v(504.47, -113.54) * mm, "end": v(504.47, -98.54) * mm});
            skLineSegment(sketch, "E139", {"start": v(444.47, -98.54) * mm, "end": v(444.47, -178.54) * mm, "construction": true});
            skLineSegment(sketch, "E140.0", {"start": v(504.47, -163.54) * mm, "end": v(444.47, -163.54) * mm, "construction": true});
            skLineSegment(sketch, "E141.0", {"start": v(459.47, -98.54) * mm, "end": v(459.47, -178.54) * mm, "construction": true});
            skCircle(sketch, "E142", {"center": v(459.47, -163.54) * mm, "radius": 2.75 * mm, "construction": true});
            skCircle(sketch, "E143.0.1.0", {"center": v(459.47, -138.54) * mm, "radius": 2.75 * mm, "construction": true});
            skCircle(sketch, "E143.0.2.0", {"center": v(459.47, -113.54) * mm, "radius": 2.75 * mm, "construction": true});
            skCircle(sketch, "E143.1.0.0", {"center": v(489.47, -163.54) * mm, "radius": 2.75 * mm, "construction": true});
            skCircle(sketch, "E143.1.1.0", {"center": v(489.47, -138.54) * mm, "radius": 2.75 * mm, "construction": true});
            skCircle(sketch, "E143.1.2.0", {"center": v(489.47, -113.54) * mm, "radius": 2.75 * mm, "construction": true});
            skLineSegment(sketch, "E143.direction1", {"start": v(459.47, -163.54) * mm, "end": v(489.47, -163.54) * mm, "construction": true});
            skLineSegment(sketch, "E143.direction2", {"start": v(459.47, -163.54) * mm, "end": v(459.47, -138.54) * mm, "construction": true});
            skCircle(sketch, "E144.MirrorC", {"center": v(899.47, -163.54) * mm, "radius": 2.75 * mm, "construction": true});
            skCircle(sketch, "E145.MirrorC", {"center": v(899.47, -138.54) * mm, "radius": 2.75 * mm, "construction": true});
            skCircle(sketch, "E146.MirrorC", {"center": v(869.47, -163.54) * mm, "radius": 2.75 * mm, "construction": true});
            skPoint(sketch, "E147.MirrorP", {"position": v(854.47, -138.54) * mm});
            skCircle(sketch, "E148.MirrorC", {"center": v(869.47, -138.54) * mm, "radius": 2.75 * mm, "construction": true});
            skLineSegment(sketch, "E149.MirrorCS", {"start": v(899.47, -163.54) * mm, "end": v(899.47, -138.54) * mm, "construction": true});
            skCircle(sketch, "E150.MirrorC", {"center": v(899.47, -113.54) * mm, "radius": 2.75 * mm, "construction": true});
            skLineSegment(sketch, "E151.MirrorCS", {"start": v(899.47, -163.54) * mm, "end": v(869.47, -163.54) * mm, "construction": true});
            skCircle(sketch, "E152.MirrorC", {"center": v(869.47, -113.54) * mm, "radius": 2.75 * mm, "construction": true});
            skLineSegment(sketch, "E153.MirrorCS", {"start": v(854.47, -163.54) * mm, "end": v(914.47, -163.54) * mm, "construction": true});
            skLineSegment(sketch, "E154.MirrorCS", {"start": v(899.47, -98.54) * mm, "end": v(899.47, -178.54) * mm, "construction": true});
            skLineSegment(sketch, "E155.MirrorCS", {"start": v(914.47, -98.54) * mm, "end": v(914.47, -178.54) * mm, "construction": true});
            skPoint(sketch, "E156.MirrorP", {"position": v(930.47, -138.54) * mm});
            skLineSegment(sketch, "E157.MirrorCS", {"start": v(930.47, -213.54) * mm, "end": v(930.47, -63.54) * mm});
            skLineSegment(sketch, "E158.MirrorCS", {"start": v(854.47, -113.54) * mm, "end": v(854.47, -98.54) * mm});
            skLineSegment(sketch, "E159.MirrorCS", {"start": v(914.47, -213.54) * mm, "end": v(914.47, -178.54) * mm});
            skLineSegment(sketch, "E160.MirrorCS", {"start": v(914.47, -98.54) * mm, "end": v(914.47, -63.54) * mm});
            skLineSegment(sketch, "E161.MirrorCS", {"start": v(854.47, -178.54) * mm, "end": v(914.47, -178.54) * mm});
            skPoint(sketch, "E162.MirrorP", {"position": v(922.47, -138.54) * mm});
            skLineSegment(sketch, "E163.MirrorCS", {"start": v(854.47, -98.54) * mm, "end": v(914.47, -98.54) * mm});
            skLineSegment(sketch, "E164.MirrorCS", {"start": v(854.47, -178.54) * mm, "end": v(854.47, -163.54) * mm});
            skLineSegment(sketch, "E165.MirrorCS", {"start": v(914.47, -213.54) * mm, "end": v(930.47, -213.54) * mm});
            skLineSegment(sketch, "E166.MirrorCS", {"start": v(914.47, -63.54) * mm, "end": v(930.47, -63.54) * mm});
            skPoint(sketch, "E167.MirrorP", {"position": v(914.47, -138.54) * mm});
            skLineSegment(sketch, "E168.MirrorCS", {"start": v(679.47, -113.54) * mm, "end": v(854.47, -113.54) * mm});
            skLineSegment(sketch, "E169.MirrorCS", {"start": v(679.47, -163.54) * mm, "end": v(854.47, -163.54) * mm});
            skLineSegment(sketch, "E170.bottom", {"start": v(714.47, -163.54) * mm, "end": v(644.47, -163.54) * mm, "construction": true});
            skLineSegment(sketch, "E170.top", {"start": v(714.47, -113.54) * mm, "end": v(644.47, -113.54) * mm, "construction": true});
            skLineSegment(sketch, "E170.left", {"start": v(714.47, -163.54) * mm, "end": v(714.47, -113.54) * mm, "construction": true});
            skLineSegment(sketch, "E170.right", {"start": v(644.47, -163.54) * mm, "end": v(644.47, -113.54) * mm, "construction": true});
            skPoint(sketch, "E170.middle", {"position": v(679.47, -138.54) * mm});
            skLineSegment(sketch, "E171.0", {"start": v(714.47, -151.54) * mm, "end": v(644.47, -151.54) * mm, "construction": true});
            skLineSegment(sketch, "E172.0", {"start": v(714.47, -123.54) * mm, "end": v(644.47, -123.54) * mm, "construction": true});
            skLineSegment(sketch, "E173.0", {"start": v(654.47, -163.54) * mm, "end": v(654.47, -113.54) * mm, "construction": true});
            skCircle(sketch, "E174", {"center": v(654.47, -123.54) * mm, "radius": 3.9 * mm, "construction": true});
            skCircle(sketch, "E175.0.1.0", {"center": v(654.47, -151.54) * mm, "radius": 3.9 * mm, "construction": true});
            skCircle(sketch, "E175.1.0.0", {"center": v(679.47, -123.54) * mm, "radius": 3.9 * mm, "construction": true});
            skCircle(sketch, "E175.2.0.0", {"center": v(704.47, -123.54) * mm, "radius": 3.9 * mm, "construction": true});
            skCircle(sketch, "E175.2.1.0", {"center": v(704.47, -151.54) * mm, "radius": 3.9 * mm, "construction": true});
            skLineSegment(sketch, "E175.direction1", {"start": v(654.47, -123.54) * mm, "end": v(679.47, -123.54) * mm, "construction": true});
            skLineSegment(sketch, "E175.direction2", {"start": v(654.47, -123.54) * mm, "end": v(654.47, -151.54) * mm, "construction": true});
            skSolve(sketch);
        }
        {
            var Q0;
            Q0 = qSketchRegion(id + "F14", true);
            var Q1;
            Q1=makeQuery(id+"F14.imprint","IMPRINT",FACE,{"disambiguationData":[TD([[makeQuery(id+"F14.imprint","IMPRINT",EDGE,{"derivedFrom":sQuery(id+"F14.wireOp",EDGE,"E132.bottom")}),-1.0]])]});
            var Q2;
            Q2=makeQuery(id+"F14.imprint","IMPRINT",FACE,{"disambiguationData":[TD([[makeQuery(id+"F14.imprint","IMPRINT",EDGE,{"derivedFrom":sQuery(id+"F14.wireOp",EDGE,"E137.left")}),-1.0]])]});
            extrude(context, id + "F15", {"entities" : qUnion([Q0, Q1, Q2]), "oppositeDirection" : true, "depth" : 10 * mm});
        }
        {
            var Q0;
            Q0=sQuery(id+"F14.wireOp",VERTEX,"E143.0.2.0.center");
            var Q1;
            Q1=sQuery(id+"F14.wireOp",VERTEX,"E143.1.2.0.center");
            var Q2;
            Q2=sQuery(id+"F14.wireOp",VERTEX,"E143.1.1.0.center");
            var Q3;
            Q3=sQuery(id+"F14.wireOp",VERTEX,"E143.direction1.end");
            var Q4;
            Q4=sQuery(id+"F14.wireOp",VERTEX,"E142.center");
            var Q5;
            Q5=sQuery(id+"F14.wireOp",VERTEX,"E143.direction2.end");
            var Q6;
            Q6=sQuery(id+"F14.wireOp",VERTEX,"E146.MirrorC.center");
            var Q7;
            Q7=sQuery(id+"F14.wireOp",VERTEX,"E148.MirrorC.center");
            var Q8;
            Q8=sQuery(id+"F14.wireOp",VERTEX,"E149.MirrorCS.start");
            var Q9;
            Q9=sQuery(id+"F14.wireOp",VERTEX,"E145.MirrorC.center");
            var Q10;
            Q10=sQuery(id+"F14.wireOp",VERTEX,"E152.MirrorC.center");
            var Q11;
            Q11=sQuery(id+"F14.wireOp",VERTEX,"E150.MirrorC.center");
            var Q12;
            Q12=makeQuery(id+"F15.opExtrude","SWEPT_BODY",BODY,{"disambiguationData":[OSD([sQuery(id+"F14.wireOp",EDGE,"E132.bottom"),sQuery(id+"F14.wireOp",EDGE,"E132.top"),sQuery(id+"F14.wireOp",EDGE,"E132.left"),sQuery(id+"F14.wireOp",EDGE,"E132.right"),sQuery(id+"F14.wireOp",EDGE,"E134.bottom"),sQuery(id+"F14.wireOp",EDGE,"E134.top"),sQuery(id+"F14.wireOp",EDGE,"E134.left"),sQuery(id+"F14.wireOp",EDGE,"E135.trimOffspring"),sQuery(id+"F14.wireOp",EDGE,"E137.bottom"),sQuery(id+"F14.wireOp",EDGE,"E137.top"),sQuery(id+"F14.wireOp",EDGE,"E137.left"),sQuery(id+"F14.wireOp",EDGE,"E138.trimOffspring")])]});
            hole(context, id + "F16", {"style" : HoleStyle.C_BORE, "endStyle" : HoleEndStyle.THROUGH, "holeDiameter" : 6 * mm, "cBoreDiameter" : 9.5 * mm, "cBoreDepth" : 4.1 * mm, "locations" : qUnion([Q0, Q1, Q2, Q3, Q4, Q5, Q6, Q7, Q8, Q9, Q10, Q11]), "scope" : qUnion([Q12]), "isTappedThrough" : true});
        }
        {
            var Q0;
            Q0=sQuery(id+"F14.wireOp",VERTEX,"E174.center");
            var Q1;
            Q1=sQuery(id+"F14.wireOp",VERTEX,"E175.direction1.end");
            var Q2;
            Q2=sQuery(id+"F14.wireOp",VERTEX,"E175.2.0.0.center");
            var Q3;
            Q3=sQuery(id+"F14.wireOp",VERTEX,"E175.2.1.0.center");
            var Q4;
            Q4=sQuery(id+"F14.wireOp",VERTEX,"E175.0.1.0.center");
            var Q5;
            Q5=makeQuery(id+"F15.opExtrude","SWEPT_BODY",BODY,{"disambiguationData":[OSD([sQuery(id+"F14.wireOp",EDGE,"E132.bottom"),sQuery(id+"F14.wireOp",EDGE,"E132.top"),sQuery(id+"F14.wireOp",EDGE,"E132.left"),sQuery(id+"F14.wireOp",EDGE,"E132.right"),sQuery(id+"F14.wireOp",EDGE,"E134.bottom"),sQuery(id+"F14.wireOp",EDGE,"E134.top"),sQuery(id+"F14.wireOp",EDGE,"E134.left"),sQuery(id+"F14.wireOp",EDGE,"E135.trimOffspring"),sQuery(id+"F14.wireOp",EDGE,"E137.bottom"),sQuery(id+"F14.wireOp",EDGE,"E137.top"),sQuery(id+"F14.wireOp",EDGE,"E138.trimOffspring"),sQuery(id+"F14.wireOp",EDGE,"E157.MirrorCS"),sQuery(id+"F14.wireOp",EDGE,"E158.MirrorCS"),sQuery(id+"F14.wireOp",EDGE,"E159.MirrorCS"),sQuery(id+"F14.wireOp",EDGE,"E160.MirrorCS"),sQuery(id+"F14.wireOp",EDGE,"E161.MirrorCS"),sQuery(id+"F14.wireOp",EDGE,"E163.MirrorCS"),sQuery(id+"F14.wireOp",EDGE,"E164.MirrorCS"),sQuery(id+"F14.wireOp",EDGE,"E165.MirrorCS"),sQuery(id+"F14.wireOp",EDGE,"E166.MirrorCS"),sQuery(id+"F14.wireOp",EDGE,"E168.MirrorCS"),sQuery(id+"F14.wireOp",EDGE,"E169.MirrorCS")])]});
            hole(context, id + "F17", {"style" : HoleStyle.C_BORE, "endStyle" : HoleEndStyle.BLIND, "holeDiameter" : 8 * mm, "cBoreDiameter" : 11 * mm, "cBoreDepth" : 5 * mm, "holeDepth" : 10 * mm, "locations" : qUnion([Q0, Q1, Q2, Q3, Q4]), "scope" : qUnion([Q5])});
        }
        {
            var Q0;
            Q0=makeQuery(id+"F15.opExtrude","SWEPT_EDGE",EDGE,{"disambiguationData":[OSD([sQuery(id+"F14.wireOp",EDGE,"E132.left"),sQuery(id+"F14.wireOp",EDGE,"E134.bottom")])]});
            var Q1;
            Q1=makeQuery(id+"F15.opExtrude","SWEPT_EDGE",EDGE,{"disambiguationData":[OSD([sQuery(id+"F14.wireOp",EDGE,"E134.top"),sQuery(id+"F14.wireOp",EDGE,"E135.trimOffspring")])]});
            var Q2;
            Q2=makeQuery(id+"F15.opExtrude","SWEPT_EDGE",EDGE,{"disambiguationData":[OSD([sQuery(id+"F14.wireOp",EDGE,"E137.top"),sQuery(id+"F14.wireOp",EDGE,"E138.trimOffspring")])]});
            var Q3;
            Q3=makeQuery(id+"F15.opExtrude","SWEPT_EDGE",EDGE,{"disambiguationData":[OSD([sQuery(id+"F14.wireOp",EDGE,"E134.left"),sQuery(id+"F14.wireOp",EDGE,"E137.bottom")])]});
            var Q4;
            Q4=makeQuery(id+"F15.opExtrude","SWEPT_EDGE",EDGE,{"disambiguationData":[OSD([sQuery(id+"F14.wireOp",EDGE,"E164.MirrorCS"),sQuery(id+"F14.wireOp",EDGE,"E169.MirrorCS")])]});
            var Q5;
            Q5=makeQuery(id+"F15.opExtrude","SWEPT_EDGE",EDGE,{"disambiguationData":[OSD([sQuery(id+"F14.wireOp",EDGE,"E158.MirrorCS"),sQuery(id+"F14.wireOp",EDGE,"E168.MirrorCS")])]});
            var Q6;
            Q6=makeQuery(id+"F15.opExtrude","SWEPT_EDGE",EDGE,{"disambiguationData":[OSD([sQuery(id+"F14.wireOp",EDGE,"E159.MirrorCS"),sQuery(id+"F14.wireOp",EDGE,"E161.MirrorCS")])]});
            var Q7;
            Q7=makeQuery(id+"F15.opExtrude","SWEPT_EDGE",EDGE,{"disambiguationData":[OSD([sQuery(id+"F14.wireOp",EDGE,"E160.MirrorCS"),sQuery(id+"F14.wireOp",EDGE,"E163.MirrorCS")])]});
            fillet(context, id + "F18", {"entities" : qUnion([Q0, Q1, Q2, Q3, Q4, Q5, Q6, Q7]), "radius" : 5 * mm, "tangentPropagation" : true, "allowEdgeOverflow" : false});
        }
        {
            var Q0;
            Q0=makeQuery(id+"F15.opExtrude","SWEPT_EDGE",EDGE,{"disambiguationData":[OSD([sQuery(id+"F14.wireOp",EDGE,"E159.MirrorCS"),sQuery(id+"F14.wireOp",EDGE,"E165.MirrorCS")])]});
            var Q1;
            Q1=makeQuery(id+"F15.opExtrude","SWEPT_EDGE",EDGE,{"disambiguationData":[OSD([sQuery(id+"F14.wireOp",EDGE,"E157.MirrorCS"),sQuery(id+"F14.wireOp",EDGE,"E165.MirrorCS")])]});
            var Q2;
            Q2=makeQuery(id+"F15.opExtrude","SWEPT_EDGE",EDGE,{"disambiguationData":[OSD([sQuery(id+"F14.wireOp",EDGE,"E157.MirrorCS"),sQuery(id+"F14.wireOp",EDGE,"E166.MirrorCS")])]});
            var Q3;
            Q3=makeQuery(id+"F15.opExtrude","SWEPT_EDGE",EDGE,{"disambiguationData":[OSD([sQuery(id+"F14.wireOp",EDGE,"E160.MirrorCS"),sQuery(id+"F14.wireOp",EDGE,"E166.MirrorCS")])]});
            var Q4;
            Q4=makeQuery(id+"F15.opExtrude","SWEPT_EDGE",EDGE,{"disambiguationData":[OSD([sQuery(id+"F14.wireOp",EDGE,"E158.MirrorCS"),sQuery(id+"F14.wireOp",EDGE,"E163.MirrorCS")])]});
            var Q5;
            Q5=makeQuery(id+"F15.opExtrude","SWEPT_EDGE",EDGE,{"disambiguationData":[OSD([sQuery(id+"F14.wireOp",EDGE,"E161.MirrorCS"),sQuery(id+"F14.wireOp",EDGE,"E164.MirrorCS")])]});
            var Q6;
            Q6=makeQuery(id+"F15.opExtrude","SWEPT_EDGE",EDGE,{"disambiguationData":[OSD([sQuery(id+"F14.wireOp",EDGE,"E134.bottom"),sQuery(id+"F14.wireOp",EDGE,"E134.left")])]});
            var Q7;
            Q7=makeQuery(id+"F15.opExtrude","SWEPT_EDGE",EDGE,{"disambiguationData":[OSD([sQuery(id+"F14.wireOp",EDGE,"E134.top"),sQuery(id+"F14.wireOp",EDGE,"E138.trimOffspring")])]});
            var Q8;
            Q8=makeQuery(id+"F15.opExtrude","SWEPT_EDGE",EDGE,{"disambiguationData":[OSD([sQuery(id+"F14.wireOp",EDGE,"E132.top"),sQuery(id+"F14.wireOp",EDGE,"E135.trimOffspring")])]});
            var Q9;
            Q9=makeQuery(id+"F15.opExtrude","SWEPT_EDGE",EDGE,{"disambiguationData":[OSD([sQuery(id+"F14.wireOp",EDGE,"E132.bottom"),sQuery(id+"F14.wireOp",EDGE,"E132.left")])]});
            var Q10;
            Q10=makeQuery(id+"F15.opExtrude","SWEPT_EDGE",EDGE,{"disambiguationData":[OSD([sQuery(id+"F14.wireOp",EDGE,"E132.bottom"),sQuery(id+"F14.wireOp",EDGE,"E132.right")])]});
            var Q11;
            Q11=makeQuery(id+"F15.opExtrude","SWEPT_EDGE",EDGE,{"disambiguationData":[OSD([sQuery(id+"F14.wireOp",EDGE,"E132.top"),sQuery(id+"F14.wireOp",EDGE,"E132.right")])]});
            fillet(context, id + "F19", {"entities" : qUnion([Q0, Q1, Q2, Q3, Q4, Q5, Q6, Q7, Q8, Q9, Q10, Q11]), "radius" : 3 * mm, "tangentPropagation" : true, "allowEdgeOverflow" : false});
        }
        {
            var Q0;
            Q0=qCreatedBy(makeId("Front.planeOp"),FACE);
            var sketch = newSketch(context, id + "F20", { "sketchPlane" : qUnion([Q0])});
            skLineSegment(sketch, "E176.bottom", {"start": v(-330.7, -236.38) * mm, "end": v(-350.7, -236.38) * mm});
            skLineSegment(sketch, "E176.top", {"start": v(-330.7, -216.38) * mm, "end": v(-350.7, -216.38) * mm});
            skLineSegment(sketch, "E176.left", {"start": v(-330.7, -236.38) * mm, "end": v(-330.7, -216.38) * mm});
            skLineSegment(sketch, "E176.right", {"start": v(-350.7, -236.38) * mm, "end": v(-350.7, -216.38) * mm});
            skPoint(sketch, "E176.middle", {"position": v(-340.7, -226.38) * mm});
            skCircle(sketch, "E177", {"center": v(-340.7, -226.38) * mm, "radius": 2.5 * mm});
            skSolve(sketch);
        }
        {
            var Q0;
            Q0=makeQuery(id+"F20.imprint","IMPRINT",FACE,{"disambiguationData":[TD([[makeQuery(id+"F20.imprint","IMPRINT",EDGE,{"derivedFrom":sQuery(id+"F20.wireOp",EDGE,"E176.bottom")}),-1.0]])]});
            extrude(context, id + "F21", {"entities" : qUnion([Q0]), "oppositeDirection" : true, "depth" : 470 * mm});
        }
        {
            var Q0;
            Q0=makeQuery(id+"F21.opExtrude","SWEPT_EDGE",EDGE,{"disambiguationData":[OSD([sQuery(id+"F20.wireOp",EDGE,"E176.top"),sQuery(id+"F20.wireOp",EDGE,"E176.right")])]});
            var Q1;
            Q1=makeQuery(id+"F21.opExtrude","SWEPT_EDGE",EDGE,{"disambiguationData":[OSD([sQuery(id+"F20.wireOp",EDGE,"E176.top"),sQuery(id+"F20.wireOp",EDGE,"E176.left")])]});
            var Q2;
            Q2=makeQuery(id+"F21.opExtrude","SWEPT_EDGE",EDGE,{"disambiguationData":[OSD([sQuery(id+"F20.wireOp",EDGE,"E176.bottom"),sQuery(id+"F20.wireOp",EDGE,"E176.left")])]});
            var Q3;
            Q3=makeQuery(id+"F21.opExtrude","SWEPT_EDGE",EDGE,{"disambiguationData":[OSD([sQuery(id+"F20.wireOp",EDGE,"E176.bottom"),sQuery(id+"F20.wireOp",EDGE,"E176.right")])]});
            fillet(context, id + "F22", {"entities" : qUnion([Q0, Q1, Q2, Q3]), "radius" : 3 * mm, "tangentPropagation" : true, "allowEdgeOverflow" : false});
        }
        {
            var Q0;
            Q0=qCreatedBy(makeId("Front.planeOp"),FACE);
            var sketch = newSketch(context, id + "F23", { "sketchPlane" : qUnion([Q0])});
            skLineSegment(sketch, "E178.bottom", {"start": v(-852.03, 400.92) * mm, "end": v(-388.03, 400.92) * mm});
            skLineSegment(sketch, "E178.top", {"start": v(-852.03, 300.92) * mm, "end": v(-388.03, 300.92) * mm});
            skLineSegment(sketch, "E178.left", {"start": v(-855.03, 397.92) * mm, "end": v(-855.03, 303.92) * mm});
            skLineSegment(sketch, "E178.right", {"start": v(-385.03, 397.92) * mm, "end": v(-385.03, 303.92) * mm});
            skPoint(sketch, "E179.visualSharp", {"position": v(-855.03, 400.92) * mm});
            skArc(sketch, "E179.filletArc", {"start": v(-852.03, 400.92) * mm, "mid": v(-854.15, 400.04) * mm, "end": v(-855.03, 397.92) * mm});
            skPoint(sketch, "E180.visualSharp", {"position": v(-855.03, 300.92) * mm});
            skArc(sketch, "E180.filletArc", {"start": v(-855.03, 303.92) * mm, "mid": v(-854.15, 301.8) * mm, "end": v(-852.03, 300.92) * mm});
            skPoint(sketch, "E181.visualSharp", {"position": v(-385.03, 300.92) * mm});
            skArc(sketch, "E181.filletArc", {"start": v(-388.03, 300.92) * mm, "mid": v(-385.91, 301.8) * mm, "end": v(-385.03, 303.92) * mm});
            skPoint(sketch, "E182.visualSharp", {"position": v(-385.03, 400.92) * mm});
            skArc(sketch, "E182.filletArc", {"start": v(-385.03, 397.92) * mm, "mid": v(-385.91, 400.04) * mm, "end": v(-388.03, 400.92) * mm});
            skSolve(sketch);
        }
        {
            var Q0;
            Q0=makeQuery(id+"F23.imprint","IMPRINT",FACE,{"disambiguationData":[TD([[makeQuery(id+"F23.imprint","IMPRINT",EDGE,{"derivedFrom":sQuery(id+"F23.wireOp",EDGE,"E178.bottom")}),-1.0]])]});
            extrude(context, id + "F24", {"entities" : qUnion([Q0]), "oppositeDirection" : true, "depth" : 16 * mm});
        }
        {
            var Q0;
            Q0=makeQuery(id+"F24.opExtrude","SWEPT_FACE",FACE,{"disambiguationData":[OSD([sQuery(id+"F23.wireOp",EDGE,"E178.right")])]});
            var sketch = newSketch(context, id + "F25", { "sketchPlane" : qUnion([Q0])});
            skLineSegment(sketch, "E183.0", {"start": v(16, 310.92) * mm, "end": v(0, 310.92) * mm, "construction": true});
            skCircle(sketch, "E184", {"center": v(8, 310.92) * mm, "radius": 4 * mm, "construction": true});
            skCircle(sketch, "E185.0.1.0", {"center": v(8, 335.92) * mm, "radius": 4 * mm, "construction": true});
            skCircle(sketch, "E185.0.2.0", {"center": v(8, 360.92) * mm, "radius": 4 * mm, "construction": true});
            skCircle(sketch, "E185.0.3.0", {"center": v(8, 385.92) * mm, "radius": 4 * mm, "construction": true});
            skLineSegment(sketch, "E185.direction1", {"start": v(8, 310.92) * mm, "end": v(33, 310.92) * mm, "construction": true});
            skLineSegment(sketch, "E185.direction2", {"start": v(8, 310.92) * mm, "end": v(8, 335.92) * mm, "construction": true});
            skSolve(sketch);
        }
        {
            var Q0;
            Q0=sQuery(id+"F25.wireOp",VERTEX,"E185.0.3.0.center");
            var Q1;
            Q1=sQuery(id+"F25.wireOp",VERTEX,"E185.0.2.0.center");
            var Q2;
            Q2=sQuery(id+"F25.wireOp",VERTEX,"E185.0.1.0.center");
            var Q3;
            Q3=sQuery(id+"F25.wireOp",VERTEX,"E184.center");
            var Q4;
            Q4=makeQuery(id+"F24.opExtrude","SWEPT_BODY",BODY,{"disambiguationData":[OSD([sQuery(id+"F23.wireOp",EDGE,"E178.bottom"),sQuery(id+"F23.wireOp",EDGE,"E178.top"),sQuery(id+"F23.wireOp",EDGE,"E178.left"),sQuery(id+"F23.wireOp",EDGE,"E178.right"),sQuery(id+"F23.wireOp",EDGE,"E179.filletArc"),sQuery(id+"F23.wireOp",EDGE,"E180.filletArc"),sQuery(id+"F23.wireOp",EDGE,"E181.filletArc"),sQuery(id+"F23.wireOp",EDGE,"E182.filletArc")])]});
            hole(context, id + "F26", {"style" : HoleStyle.SIMPLE, "endStyle" : HoleEndStyle.THROUGH, "holeDiameter" : 8 * mm, "locations" : qUnion([Q0, Q1, Q2, Q3]), "scope" : qUnion([Q4]), "isTappedThrough" : true});
        }
        {
            var Q0;
            Q0=qCreatedBy(makeId("Front.planeOp"),FACE);
            var sketch = newSketch(context, id + "F27", { "sketchPlane" : qUnion([Q0])});
            skLineSegment(sketch, "E186.bottom", {"start": v(-452.13, -10) * mm, "end": v(-1452.13, -10) * mm});
            skLineSegment(sketch, "E186.top", {"start": v(-472.13, 10) * mm, "end": v(-520.13, 10) * mm});
            skLineSegment(sketch, "E186.left", {"start": v(-452.13, -10) * mm, "end": v(-452.13, 10) * mm});
            skLineSegment(sketch, "E186.right", {"start": v(-1452.13, -10) * mm, "end": v(-1452.13, 10) * mm});
            skPoint(sketch, "E186.middle", {"position": v(-952.13, 0) * mm});
            skLineSegment(sketch, "E187.0", {"start": v(-462.13, 40) * mm, "end": v(-462.13, 81) * mm, "construction": true});
            skLineSegment(sketch, "E188.bottom", {"start": v(-452.13, -10) * mm, "end": v(-472.13, -10) * mm});
            skLineSegment(sketch, "E188.top", {"start": v(-452.13, 90) * mm, "end": v(-472.13, 90) * mm});
            skLineSegment(sketch, "E188.left", {"start": v(-452.13, -10) * mm, "end": v(-452.13, 90) * mm});
            skLineSegment(sketch, "E188.right", {"start": v(-472.13, 10) * mm, "end": v(-472.13, 90) * mm});
            skPoint(sketch, "E188.middle", {"position": v(-462.13, 40) * mm});
            skLineSegment(sketch, "E189.bottom", {"start": v(-1452.13, -10) * mm, "end": v(-1432.13, -10) * mm});
            skLineSegment(sketch, "E189.top", {"start": v(-1452.13, 90) * mm, "end": v(-1432.13, 90) * mm});
            skLineSegment(sketch, "E189.left", {"start": v(-1452.13, -10) * mm, "end": v(-1452.13, 90) * mm});
            skLineSegment(sketch, "E189.right", {"start": v(-1432.13, 10) * mm, "end": v(-1432.13, 90) * mm});
            skPoint(sketch, "E189.middle", {"position": v(-1442.13, 40) * mm});
            skLineSegment(sketch, "E190.0", {"start": v(-1215.94, 72.5) * mm, "end": v(-1215.94, -10) * mm, "construction": true});
            skLineSegment(sketch, "E191.bottom", {"start": v(-1198.55, -10) * mm, "end": v(-1238.55, -10) * mm});
            skPoint(sketch, "E191.middle", {"position": v(-1215.94, 10) * mm});
            skLineSegment(sketch, "E192.bottom", {"start": v(-562.13, -10) * mm, "end": v(-522.13, -10) * mm});
            skPoint(sketch, "E192.middle", {"position": v(-540.13, 10) * mm});
            skLineSegment(sketch, "E193.trimOffspring", {"start": v(-560.13, 10) * mm, "end": v(-1195.94, 10) * mm});
            skLineSegment(sketch, "E194.trimOffspring", {"start": v(-1235.94, 10) * mm, "end": v(-1432.13, 10) * mm});
            skLineSegment(sketch, "E195", {"start": v(-1195.94, 10) * mm, "end": v(-1235.94, 10) * mm});
            skPoint(sketch, "E191.left.end.orphan", {"position": v(-1193.34, 30) * mm});
            skPoint(sketch, "E191.right.end.orphan", {"position": v(-1233.34, 30) * mm});
            skLineSegment(sketch, "E196", {"start": v(-520.13, 10) * mm, "end": v(-560.13, 10) * mm});
            skCircle(sketch, "E197", {"center": v(-952.13, 0) * mm, "radius": 5.5 * mm, "construction": true});
            skCircle(sketch, "E198.1.0.0", {"center": v(-707.13, 0) * mm, "radius": 5.5 * mm, "construction": true});
            skCircle(sketch, "E198.2.0.0", {"center": v(-462.13, 0) * mm, "radius": 5.5 * mm, "construction": true});
            skLineSegment(sketch, "E198.direction1", {"start": v(-952.13, 0) * mm, "end": v(-707.13, 0) * mm, "construction": true});
            skLineSegment(sketch, "E199", {"start": v(-452.13, 10) * mm, "end": v(-472.13, -10) * mm, "construction": true});
            skLineSegment(sketch, "E200", {"start": v(-472.13, 10) * mm, "end": v(-452.13, -10) * mm, "construction": true});
            skCircle(sketch, "E201.1.0.0", {"center": v(-1197.13, 0) * mm, "radius": 5.5 * mm, "construction": true});
            skCircle(sketch, "E201.2.0.0", {"center": v(-1442.13, 0) * mm, "radius": 5.5 * mm, "construction": true});
            skLineSegment(sketch, "E201.direction1", {"start": v(-952.13, 0) * mm, "end": v(-1197.13, 0) * mm, "construction": true});
            skCircle(sketch, "E202.0.1.0", {"center": v(-462.13, 25) * mm, "radius": 5.5 * mm, "construction": true});
            skCircle(sketch, "E202.0.2.0", {"center": v(-462.13, 50) * mm, "radius": 5.5 * mm, "construction": true});
            skCircle(sketch, "E202.0.3.0", {"center": v(-462.13, 75) * mm, "radius": 5.5 * mm, "construction": true});
            skLineSegment(sketch, "E202.direction1", {"start": v(-467.13, 0) * mm, "end": v(-462.13, 0) * mm, "construction": true});
            skLineSegment(sketch, "E202.direction2", {"start": v(-462.13, 0) * mm, "end": v(-462.13, 25) * mm, "construction": true});
            skCircle(sketch, "E203.0.1.0", {"center": v(-1442.13, 25) * mm, "radius": 5.5 * mm, "construction": true});
            skCircle(sketch, "E203.0.2.0", {"center": v(-1442.13, 50) * mm, "radius": 5.5 * mm, "construction": true});
            skCircle(sketch, "E203.0.3.0", {"center": v(-1442.13, 75) * mm, "radius": 5.5 * mm, "construction": true});
            skLineSegment(sketch, "E203.direction1", {"start": v(-1442.13, 0) * mm, "end": v(-1387.13, 0) * mm, "construction": true});
            skLineSegment(sketch, "E203.direction2", {"start": v(-1442.13, 0) * mm, "end": v(-1442.13, 25) * mm, "construction": true});
            skLineSegment(sketch, "E204", {"start": v(-1402.13, 10) * mm, "end": v(-1402.13, -10) * mm, "construction": true});
            skCircle(sketch, "E205", {"center": v(-1402.13, 0) * mm, "radius": 4 * mm, "construction": true});
            skCircle(sketch, "E206.1.0.0", {"center": v(-1387.13, 0) * mm, "radius": 4 * mm, "construction": true});
            skCircle(sketch, "E206.2.0.0", {"center": v(-1372.13, 0) * mm, "radius": 4 * mm, "construction": true});
            skLineSegment(sketch, "E206.direction1", {"start": v(-1402.13, 0) * mm, "end": v(-1387.13, 0) * mm, "construction": true});
            skSolve(sketch);
        }
        {
            var Q0;
            Q0 = qSketchRegion(id + "F27", true);
            extrude(context, id + "F28", {"entities" : qUnion([Q0]), "oppositeDirection" : true, "depth" : 16 * mm});
        }
        {
            var Q0;
            Q0=sQuery(id+"F27.wireOp",VERTEX,"E201.2.0.0.center");
            var Q1;
            Q1=sQuery(id+"F27.wireOp",VERTEX,"E203.direction2.end");
            var Q2;
            Q2=sQuery(id+"F27.wireOp",VERTEX,"E203.0.2.0.center");
            var Q3;
            Q3=sQuery(id+"F27.wireOp",VERTEX,"E203.0.3.0.center");
            var Q4;
            Q4=sQuery(id+"F27.wireOp",VERTEX,"E201.direction1.end");
            var Q5;
            Q5=sQuery(id+"F27.wireOp",VERTEX,"E186.middle");
            var Q6;
            Q6=sQuery(id+"F27.wireOp",VERTEX,"E198.1.0.0.center");
            var Q7;
            Q7=sQuery(id+"F27.wireOp",VERTEX,"E202.direction1.start");
            var Q8;
            Q8=sQuery(id+"F27.wireOp",VERTEX,"E202.direction2.end");
            var Q9;
            Q9=sQuery(id+"F27.wireOp",VERTEX,"E202.0.2.0.center");
            var Q10;
            Q10=sQuery(id+"F27.wireOp",VERTEX,"E202.0.3.0.center");
            var Q11;
            Q11=sQuery(id+"F27.wireOp",VERTEX,"E206.1.0.0.center");
            var Q12;
            Q12=sQuery(id+"F27.wireOp",VERTEX,"E206.2.0.0.center");
            var Q13;
            Q13=sQuery(id+"F27.wireOp",VERTEX,"E206.direction1.start");
            var Q14;
            Q14=makeQuery(id+"F28.opExtrude","SWEPT_BODY",BODY,{"disambiguationData":[OSD([sQuery(id+"F27.wireOp",EDGE,"E186.bottom"),sQuery(id+"F27.wireOp",EDGE,"E186.top"),sQuery(id+"F27.wireOp",EDGE,"E188.bottom"),sQuery(id+"F27.wireOp",EDGE,"E188.top"),sQuery(id+"F27.wireOp",EDGE,"E188.left"),sQuery(id+"F27.wireOp",EDGE,"E188.right"),sQuery(id+"F27.wireOp",EDGE,"E189.bottom"),sQuery(id+"F27.wireOp",EDGE,"E189.top"),sQuery(id+"F27.wireOp",EDGE,"E189.left"),sQuery(id+"F27.wireOp",EDGE,"E189.right"),sQuery(id+"F27.wireOp",EDGE,"E191.bottom"),sQuery(id+"F27.wireOp",EDGE,"E192.bottom"),sQuery(id+"F27.wireOp",EDGE,"E193.trimOffspring"),sQuery(id+"F27.wireOp",EDGE,"E194.trimOffspring"),sQuery(id+"F27.wireOp",EDGE,"E195"),sQuery(id+"F27.wireOp",EDGE,"E196")])]});
            hole(context, id + "F29", {"style" : HoleStyle.C_BORE, "endStyle" : HoleEndStyle.THROUGH, "holeDiameter" : 8 * mm, "cBoreDiameter" : 11 * mm, "cBoreDepth" : 4 * mm, "locations" : qUnion([Q0, Q1, Q2, Q3, Q4, Q5, Q6, Q7, Q8, Q9, Q10, Q11, Q12, Q13]), "scope" : qUnion([Q14]), "isTappedThrough" : true});
        }
        {
            var Q0;
            Q0=qCreatedBy(makeId("Front.planeOp"),FACE);
            var sketch = newSketch(context, id + "F30", { "sketchPlane" : qUnion([Q0])});
            skLineSegment(sketch, "E207.bottom", {"start": v(-1329.5, -106.63) * mm, "end": v(-1349.5, -106.63) * mm});
            skLineSegment(sketch, "E207.top", {"start": v(-1329.5, -86.63) * mm, "end": v(-1349.5, -86.63) * mm});
            skLineSegment(sketch, "E207.left", {"start": v(-1329.5, -106.63) * mm, "end": v(-1329.5, -86.63) * mm});
            skLineSegment(sketch, "E207.right", {"start": v(-1349.5, -106.63) * mm, "end": v(-1349.5, -86.63) * mm});
            skPoint(sketch, "E207.middle", {"position": v(-1339.5, -96.63) * mm});
            skCircle(sketch, "E208", {"center": v(-1339.5, -96.63) * mm, "radius": 4 * mm});
            skSolve(sketch);
        }
        {
            var Q0;
            Q0=makeQuery(id+"F30.imprint","IMPRINT",FACE,{"disambiguationData":[TD([[makeQuery(id+"F30.imprint","IMPRINT",EDGE,{"derivedFrom":sQuery(id+"F30.wireOp",EDGE,"E207.bottom")}),-1.0]])]});
            extrude(context, id + "F31", {"entities" : qUnion([Q0]), "oppositeDirection" : true, "depth" : 458 * mm});
        }
    });
